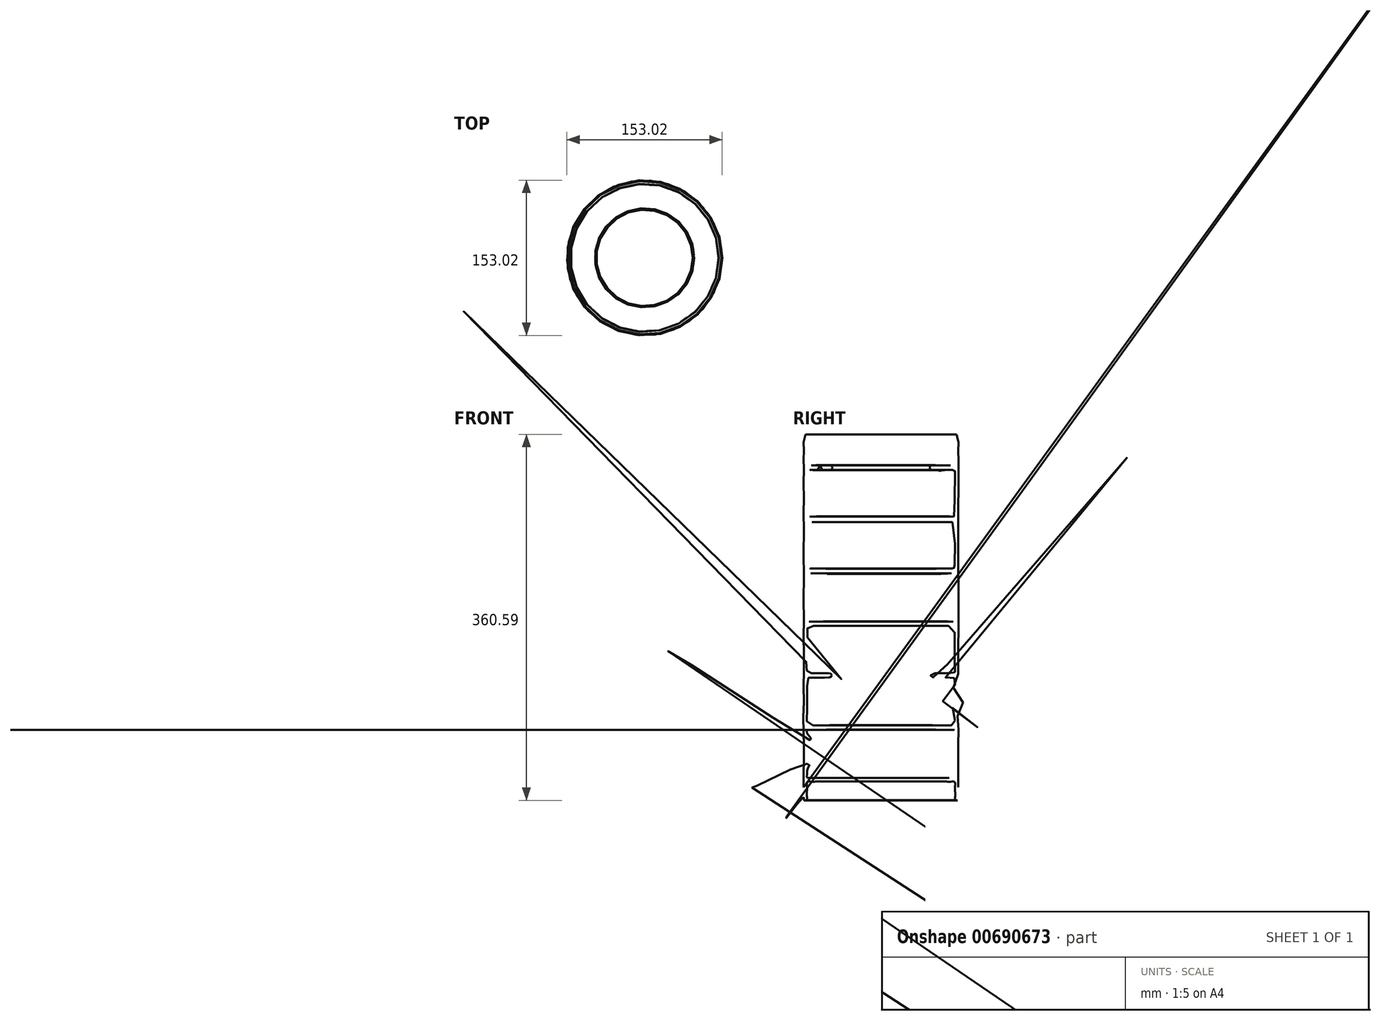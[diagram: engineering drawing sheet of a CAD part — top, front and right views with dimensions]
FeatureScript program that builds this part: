
annotation { "Feature Type Name" : "Feature", "Feature Type Description" : "" }
export const myFeature = defineFeature(function(context is Context, id is Id, definition is map)
    precondition{}
    {
        {
            var Q0;
            Q0=qCreatedBy(makeId("Front.planeOp"),FACE);
            var sketch = newSketch(context, id + "F0", { "sketchPlane" : qUnion([Q0])});
            skLineSegment(sketch, "E0", {"start": v(0, 0) * mm, "end": v(76.2, 0) * mm});
            skLineSegment(sketch, "E1", {"start": v(76.2, 0) * mm, "end": v(76.2, 8.12) * mm});
            skLineSegment(sketch, "E2.top", {"start": v(0, 355.6) * mm, "end": v(76.2, 355.6) * mm});
            skLineSegment(sketch, "E2.left", {"start": v(0, 0) * mm, "end": v(0, 355.6) * mm});
            skLineSegment(sketch, "E2.right", {"start": v(76.2, 0) * mm, "end": v(76.2, 355.6) * mm});
            skLineSegment(sketch, "E3", {"start": v(76.2, 20.38) * mm, "end": v(50.8, 20.38) * mm});
            skLineSegment(sketch, "E4.0.1.0", {"start": v(76.2, 71.68) * mm, "end": v(50.8, 71.68) * mm});
            skLineSegment(sketch, "E4.0.2.0", {"start": v(76.2, 123) * mm, "end": v(50.8, 123) * mm});
            skLineSegment(sketch, "E4.0.3.0", {"start": v(76.2, 174.3) * mm, "end": v(50.8, 174.3) * mm});
            skLineSegment(sketch, "E4.0.4.0", {"start": v(76.2, 225.6) * mm, "end": v(50.8, 225.6) * mm});
            skLineSegment(sketch, "E4.0.5.0", {"start": v(76.2, 276.92) * mm, "end": v(50.8, 276.92) * mm});
            skLineSegment(sketch, "E4.0.6.0", {"start": v(76.2, 328.22) * mm, "end": v(50.8, 328.22) * mm});
            skLineSegment(sketch, "E4.direction1", {"start": v(50.8, 20.38) * mm, "end": v(76.2, 20.38) * mm, "construction": true});
            skLineSegment(sketch, "E4.direction2", {"start": v(50.8, 20.38) * mm, "end": v(50.8, 71.68) * mm, "construction": true});
            skLineSegment(sketch, "E5.bottom", {"start": v(76.2, 0) * mm, "end": v(72.99, 0) * mm});
            skLineSegment(sketch, "E5.top", {"start": v(76.2, 355.6) * mm, "end": v(72.99, 355.6) * mm});
            skLineSegment(sketch, "E5.right", {"start": v(72.99, 0) * mm, "end": v(72.99, 355.6) * mm});
            skSolve(sketch);
        }
        {
            var Q0;
            Q0=qCreatedBy(makeId("Front.planeOp"),FACE);
            var sketch = newSketch(context, id + "F1", { "sketchPlane" : qUnion([Q0])});
            skLineSegment(sketch, "E6", {"start": v(0, 0) * mm, "end": v(0, 20.97) * mm});
            skFitSpline(sketch, "E7", {"points": [v(76.18, 12.78) * mm, v(76.15, 3.09) * mm, v(75.75, 0) * mm, v(74.28, 0) * mm, v(73.4, 0) * mm, v(73.03, 5.68) * mm, v(73.03, 11.66) * mm, v(73, 15.36) * mm, v(72.88, 17.76) * mm, v(71.7, 18.39) * mm, v(60.47, 18.6) * mm, v(52.36, 18.6) * mm, v(49.68, 19.37) * mm, v(49.62, 21.4) * mm, v(51.77, 21.97) * mm, v(71.7, 21.93) * mm, v(72.88, 22.3) * mm, v(73, 25.39) * mm, v(72.87, 46.95) * mm, v(72.97, 66.59) * mm, v(72.99, 69.17) * mm, v(71.2, 69.37) * mm, v(51.65, 69.57) * mm, v(48.49, 70.16) * mm, v(48.39, 73.4) * mm, v(52.24, 74.1) * mm, v(70.99, 73.87) * mm, v(72.79, 74.3) * mm, v(72.99, 76.28) * mm, v(72.95, 95.45) * mm, v(72.91, 115.96) * mm, v(72.72, 119.93) * mm, v(69.42, 120.78) * mm, v(50.98, 121.07) * mm, v(49, 121.92) * mm, v(49.09, 124.1) * mm, v(51.17, 125.04) * mm, v(70.27, 125.42) * mm, v(72.82, 126.36) * mm, v(72.82, 133.27) * mm, v(72.6, 168.48) * mm, v(72.08, 171.44) * mm, v(69.12, 171.95) * mm, v(51.87, 172.17) * mm, v(48.9, 173.32) * mm, v(49.38, 175.54) * mm, v(51.07, 176.18) * mm, v(68.75, 176.03) * mm, v(72.24, 176.36) * mm, v(72.97, 181.68) * mm, v(72.88, 200.44) * mm, v(72.31, 218.64) * mm, v(72.03, 222.89) * mm, v(68.63, 223.6) * mm, v(51.2, 223.03) * mm, v(48.14, 224.42) * mm, v(49.08, 227.7) * mm, v(52.94, 228.2) * mm, v(68.08, 228.46) * mm, v(72.03, 228.84) * mm, v(72.74, 233.09) * mm, v(72.83, 252.39) * mm, v(73, 270.54) * mm, v(72.21, 273.5) * mm, v(69.25, 274.1) * mm, v(50.28, 274.3) * mm, v(47.64, 275.58) * mm, v(48.08, 278.98) * mm, v(52.93, 279.71) * mm, v(67.3, 279.77) * mm, v(72.25, 280.16) * mm, v(72.75, 288.1) * mm, v(72.9, 303.64) * mm, v(72.92, 321.7) * mm, v(72.46, 325) * mm, v(68.32, 325.4) * mm, v(54.08, 325.4) * mm, v(48.45, 326.52) * mm, v(48.46, 329.18) * mm, v(53.5, 330.37) * mm, v(71.4, 330.2) * mm, v(72.68, 331.09) * mm, v(72.9, 340.33) * mm, v(72.98, 352.4) * mm, v(73.3, 357.85) * mm, v(74.38, 360.52) * mm, v(75.74, 358.6) * mm, v(76.16, 343.8) * mm, v(76.17, 330.06) * mm, v(75.82, 328.26) * mm, v(76.25, 326.03) * mm, v(76.22, 320.77) * mm, v(76.33, 312.9) * mm, v(76.17, 282.33) * mm, v(76.37, 278.56) * mm, v(75.93, 276.93) * mm, v(76.04, 272.2) * mm, v(76.28, 252.92) * mm, v(76.14, 230.54) * mm, v(75.57, 225.86) * mm, v(76, 222.32) * mm, v(76.41, 202.2) * mm, v(76.08, 177.16) * mm, v(75.57, 174.38) * mm, v(76.08, 171.98) * mm, v(76.33, 167.57) * mm, v(76.06, 150.06) * mm, v(76.24, 127.23) * mm, v(76.16, 124.93) * mm, v(75.83, 123.12) * mm, v(76.13, 120.78) * mm, v(76.36, 80.15) * mm, v(76.22, 74.29) * mm, v(75.68, 71.9) * mm, v(76.11, 70.57) * mm, v(76.18, 66.22) * mm, v(76.11, 53.08) * mm, v(76.2, 22.43) * mm, v(76.18, 21.47) * mm, v(75.97, 20.54) * mm, v(76.16, 19.57) * mm, v(76.18, 12.78) * mm]});
            skSolve(sketch);
        }
        {
            var Q0;
            Q0=makeQuery(id+"F1.imprint","IMPRINT",FACE,{"disambiguationData":[TD([[makeQuery(id+"F1.imprint","IMPRINT",EDGE,{"derivedFrom":sQuery(id+"F1.wireOp",EDGE,"E7")}),-1.0]])]});
            var Q1;
            Q1=sQuery(id+"F1.wireOp",EDGE,"b9abf473-961d-48db-87c0-f077a59cea3a");
            var Q2;
            Q2=sQuery(id+"F0.wireOp",EDGE,"E2.left");
            revolve(context, id + "F2", {"surfaceOperationType" : NewSurfaceOperationType.NEW, "entities" : qUnion([Q0]), "surfaceEntities" : qUnion([Q1]), "axis" : qUnion([Q2]), "revolveType" : RevolveType.FULL});
        }
    });
